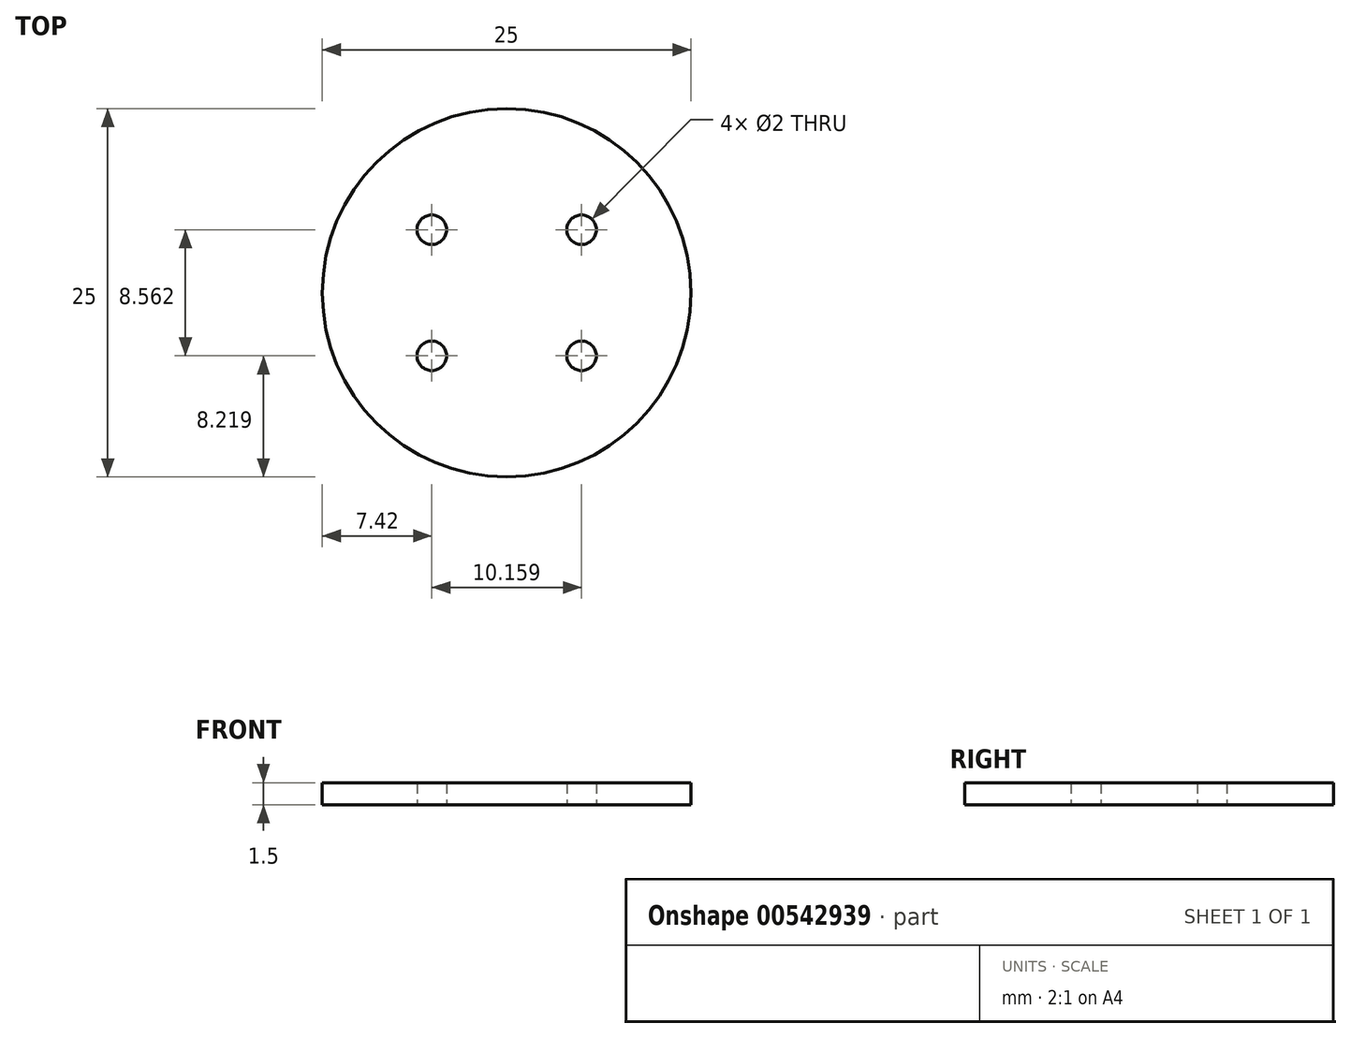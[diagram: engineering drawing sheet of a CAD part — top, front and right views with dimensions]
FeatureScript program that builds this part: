
annotation { "Feature Type Name" : "Feature", "Feature Type Description" : "" }
export const myFeature = defineFeature(function(context is Context, id is Id, definition is map)
    precondition{}
    {
        {
            var Q0;
            Q0=qCreatedBy(makeId("Top.planeOp"),FACE);
            var sketch = newSketch(context, id + "F0", { "sketchPlane" : qUnion([Q0])});
            skCircle(sketch, "E0", {"center": v(0, 0) * mm, "radius": 12.5 * mm});
            skCircle(sketch, "E1", {"center": v(-5.08, 4.28) * mm, "radius": 1 * mm});
            skCircle(sketch, "E2.MirrorC", {"center": v(-5.08, -4.28) * mm, "radius": 1 * mm});
            skCircle(sketch, "E3.MirrorC", {"center": v(5.08, 4.28) * mm, "radius": 1 * mm});
            skCircle(sketch, "E4.MirrorC", {"center": v(5.08, -4.28) * mm, "radius": 1 * mm});
            skSolve(sketch);
        }
        {
            var Q0;
            Q0=makeQuery(id+"F0.imprint","IMPRINT",FACE,{"disambiguationData":[TD([[makeQuery(id+"F0.imprint","IMPRINT",EDGE,{"derivedFrom":sQuery(id+"F0.wireOp",EDGE,"E0")}),1.0]])]});
            extrude(context, id + "F1", {"entities" : qUnion([Q0]), "depth" : 1.5 * mm, "offsetDistance" : 25 * mm});
        }
    });
